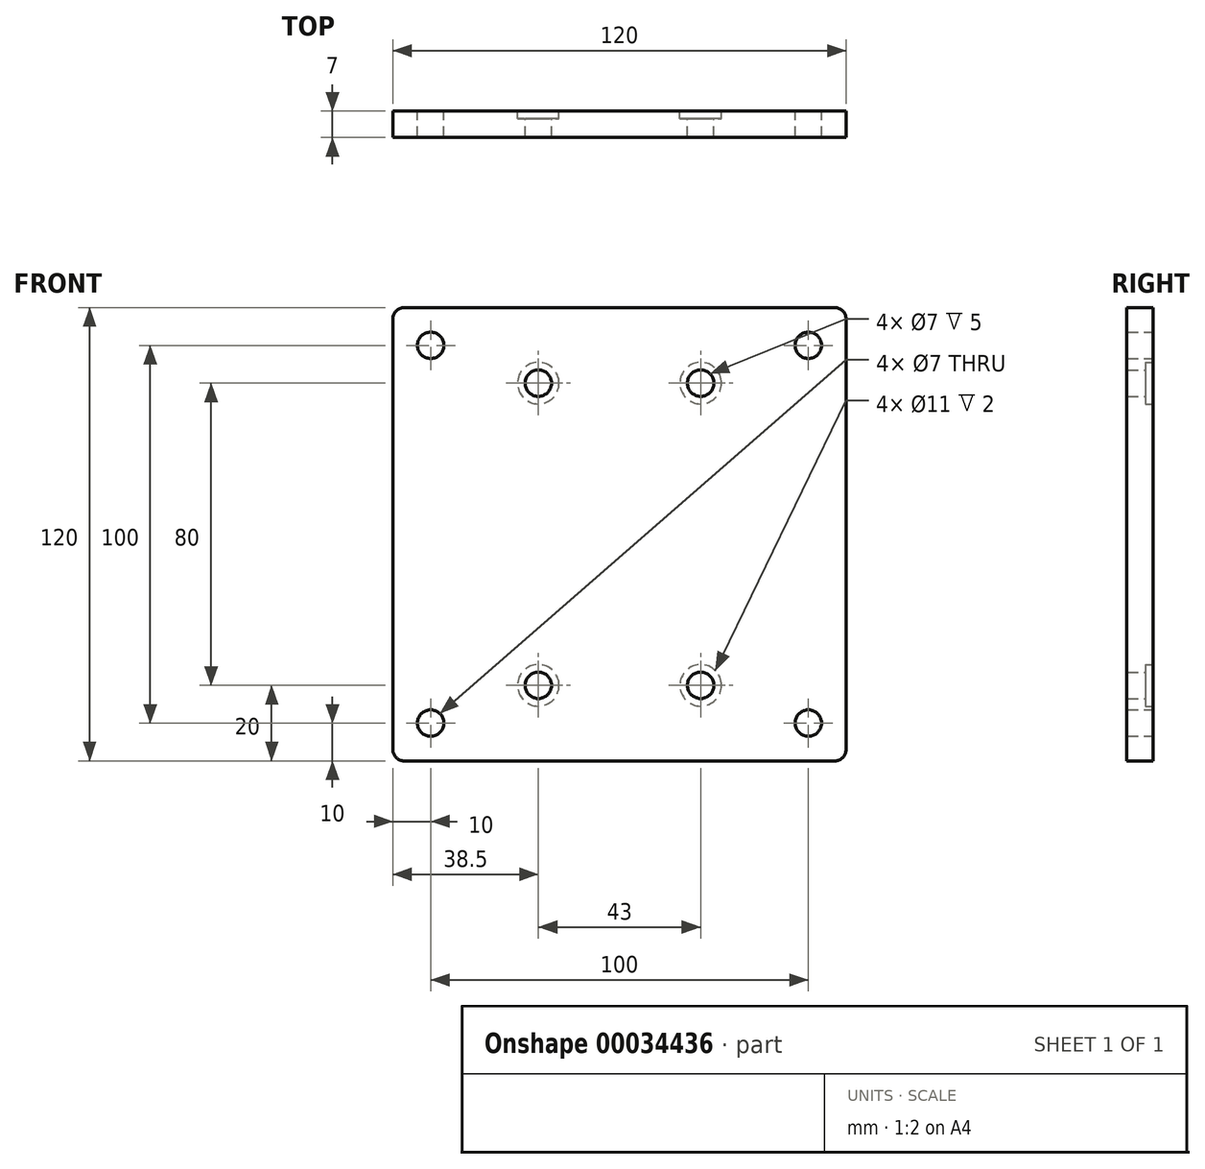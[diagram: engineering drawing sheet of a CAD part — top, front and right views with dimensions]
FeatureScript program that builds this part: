
annotation { "Feature Type Name" : "Feature", "Feature Type Description" : "" }
export const myFeature = defineFeature(function(context is Context, id is Id, definition is map)
    precondition{}
    {
        {
            var Q0;
            Q0=qCreatedBy(makeId("Front.planeOp"),FACE);
            var sketch = newSketch(context, id + "F0", { "sketchPlane" : qUnion([Q0])});
            skLineSegment(sketch, "E0.rect.bottom", {"start": v(60, -60) * mm, "end": v(-60, -60) * mm});
            skLineSegment(sketch, "E0.rect.top", {"start": v(60, 60) * mm, "end": v(-60, 60) * mm});
            skLineSegment(sketch, "E0.rect.left", {"start": v(60, -60) * mm, "end": v(60, 60) * mm});
            skLineSegment(sketch, "E0.rect.right", {"start": v(-60, -60) * mm, "end": v(-60, 60) * mm});
            skPoint(sketch, "E0.rect.middle", {"position": v(0, 0) * mm});
            skCircle(sketch, "E1", {"center": v(-50, 50) * mm, "radius": 3.5 * mm});
            skCircle(sketch, "E2", {"center": v(50, 50) * mm, "radius": 3.5 * mm});
            skCircle(sketch, "E3", {"center": v(-50, -50) * mm, "radius": 3.5 * mm});
            skCircle(sketch, "E4", {"center": v(50, -50) * mm, "radius": 3.5 * mm});
            skSolve(sketch);
        }
        {
            var Q0;
            Q0 = qSketchRegion(id + "F0", true);
            extrude(context, id + "F1", {"entities" : qUnion([Q0]), "depth" : 7 * mm});
        }
        {
            var Q0;
            Q0=makeQuery(id+"F1.opExtrude","SWEPT_EDGE",EDGE,{"disambiguationData":[OSD([sQuery(id+"F0.wireOp",EDGE,"E0.rect.top"),sQuery(id+"F0.wireOp",EDGE,"E0.rect.right")])]});
            var Q1;
            Q1=makeQuery(id+"F1.opExtrude","SWEPT_EDGE",EDGE,{"disambiguationData":[OSD([sQuery(id+"F0.wireOp",EDGE,"E0.rect.bottom"),sQuery(id+"F0.wireOp",EDGE,"E0.rect.right")])]});
            var Q2;
            Q2=makeQuery(id+"F1.opExtrude","SWEPT_EDGE",EDGE,{"disambiguationData":[OSD([sQuery(id+"F0.wireOp",EDGE,"E0.rect.bottom"),sQuery(id+"F0.wireOp",EDGE,"E0.rect.left")])]});
            var Q3;
            Q3=makeQuery(id+"F1.opExtrude","SWEPT_EDGE",EDGE,{"disambiguationData":[OSD([sQuery(id+"F0.wireOp",EDGE,"E0.rect.top"),sQuery(id+"F0.wireOp",EDGE,"E0.rect.left")])]});
            fillet(context, id + "F2", {"entities" : qUnion([Q0, Q1, Q2, Q3]), "radius" : 3 * mm, "tangentPropagation" : true, "allowEdgeOverflow" : false});
        }
        {
            var Q0;
            Q0=makeQuery(id+"F1.opExtrude","CAP_FACE",FACE,{"disambiguationData":[OSD([sQuery(id+"F0.wireOp",EDGE,"E0.rect.bottom"),sQuery(id+"F0.wireOp",EDGE,"E0.rect.top"),sQuery(id+"F0.wireOp",EDGE,"E0.rect.left"),sQuery(id+"F0.wireOp",EDGE,"E0.rect.right"),sQuery(id+"F0.wireOp",EDGE,"E1"),sQuery(id+"F0.wireOp",EDGE,"E2"),sQuery(id+"F0.wireOp",EDGE,"E3"),sQuery(id+"F0.wireOp",EDGE,"E4")])],"isStart":true});
            var sketch = newSketch(context, id + "F3", { "sketchPlane" : qUnion([Q0])});
            skLineSegment(sketch, "E5", {"start": v(-36.5, -60) * mm, "end": v(-36.5, 60) * mm, "construction": true});
            skLineSegment(sketch, "E6", {"start": v(-36.5, 60) * mm, "end": v(36.5, 60) * mm, "construction": true});
            skLineSegment(sketch, "E7", {"start": v(36.5, 60) * mm, "end": v(36.5, -60) * mm, "construction": true});
            skLineSegment(sketch, "E8", {"start": v(36.5, -60) * mm, "end": v(-36.5, -60) * mm, "construction": true});
            skLineSegment(sketch, "E9", {"start": v(-21.5, 60) * mm, "end": v(-21.5, -60) * mm, "construction": true});
            skLineSegment(sketch, "E10", {"start": v(21.5, 60) * mm, "end": v(21.5, -60) * mm, "construction": true});
            skLineSegment(sketch, "E11", {"start": v(-36.5, 40) * mm, "end": v(36.5, 40) * mm, "construction": true});
            skLineSegment(sketch, "E12", {"start": v(-36.5, -40) * mm, "end": v(36.5, -40) * mm, "construction": true});
            skCircle(sketch, "E13", {"center": v(-21.5, 40) * mm, "radius": 3.5 * mm});
            skCircle(sketch, "E14", {"center": v(21.5, 40) * mm, "radius": 3.5 * mm});
            skCircle(sketch, "E15", {"center": v(-21.5, -40) * mm, "radius": 3.5 * mm});
            skCircle(sketch, "E16", {"center": v(21.5, -40) * mm, "radius": 3.5 * mm});
            skSolve(sketch);
        }
        {
            var Q0;
            Q0 = qSketchRegion(id + "F3", true);
            extrude(context, id + "F4", {"entities" : qUnion([Q0]), "operationType" : NewBodyOperationType.REMOVE, "oppositeDirection" : true, "depth" : 25 * mm});
        }
        {
            var Q0;
            Q0=makeQuery(id+"F1.opExtrude","CAP_FACE",FACE,{"disambiguationData":[OSD([sQuery(id+"F0.wireOp",EDGE,"E0.rect.bottom"),sQuery(id+"F0.wireOp",EDGE,"E0.rect.top"),sQuery(id+"F0.wireOp",EDGE,"E0.rect.left"),sQuery(id+"F0.wireOp",EDGE,"E0.rect.right"),sQuery(id+"F0.wireOp",EDGE,"E1"),sQuery(id+"F0.wireOp",EDGE,"E2"),sQuery(id+"F0.wireOp",EDGE,"E3"),sQuery(id+"F0.wireOp",EDGE,"E4")])],"isStart":true});
            var sketch = newSketch(context, id + "F5", { "sketchPlane" : qUnion([Q0])});
            skCircle(sketch, "E17", {"center": v(-21.5, 40) * mm, "radius": 5.5 * mm});
            skCircle(sketch, "E18", {"center": v(21.5, 40) * mm, "radius": 5.5 * mm});
            skCircle(sketch, "E19", {"center": v(-21.5, -40) * mm, "radius": 5.5 * mm});
            skCircle(sketch, "E20", {"center": v(21.5, -40) * mm, "radius": 5.5 * mm});
            skSolve(sketch);
        }
        {
            var Q0;
            Q0 = qSketchRegion(id + "F5", true);
            extrude(context, id + "F6", {"entities" : qUnion([Q0]), "operationType" : NewBodyOperationType.REMOVE, "oppositeDirection" : true, "depth" : 2 * mm});
        }
    });
